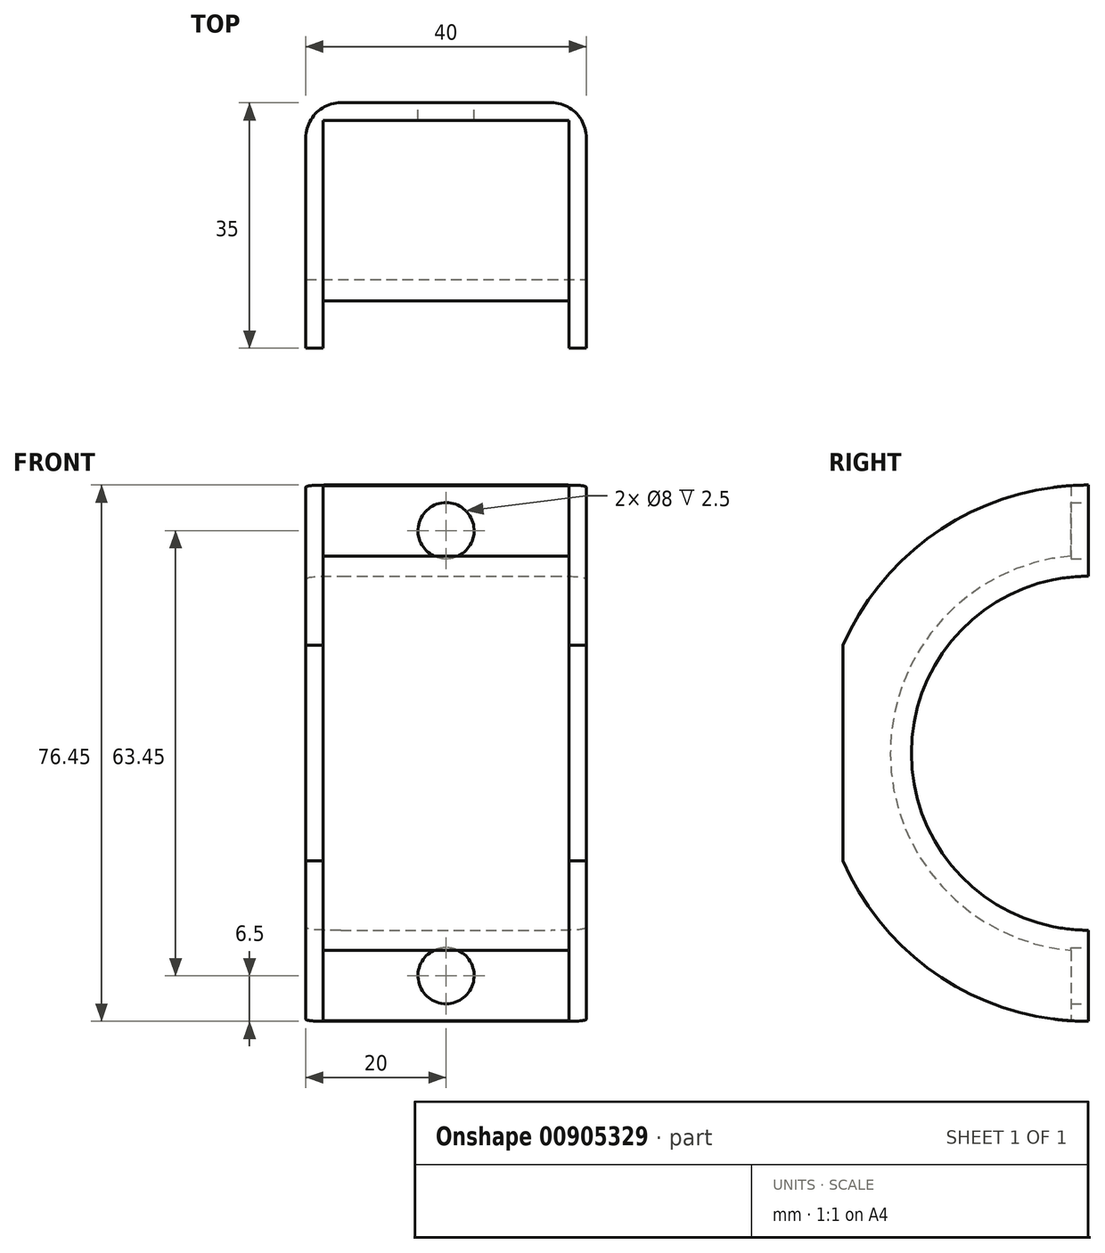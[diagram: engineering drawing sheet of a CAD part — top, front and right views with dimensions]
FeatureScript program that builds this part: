
annotation { "Feature Type Name" : "Feature", "Feature Type Description" : "" }
export const myFeature = defineFeature(function(context is Context, id is Id, definition is map)
    precondition{}
    {
        {
            var Q0;
            Q0=qCreatedBy(makeId("Top.planeOp"),FACE);
            var sketch = newSketch(context, id + "F0", { "sketchPlane" : qUnion([Q0])});
            skLineSegment(sketch, "E0.bottom", {"start": v(-20, 20) * mm, "end": v(20, 20) * mm});
            skLineSegment(sketch, "E0.top", {"start": v(-20, -20) * mm, "end": v(20, -20) * mm});
            skLineSegment(sketch, "E0.left", {"start": v(-20, 20) * mm, "end": v(-20, -20) * mm});
            skLineSegment(sketch, "E0.right", {"start": v(20, 20) * mm, "end": v(20, -20) * mm});
            skLineSegment(sketch, "E1.bottom", {"start": v(-17.5, 17.5) * mm, "end": v(17.5, 17.5) * mm});
            skLineSegment(sketch, "E1.top", {"start": v(-17.5, -17.5) * mm, "end": v(17.5, -17.5) * mm});
            skLineSegment(sketch, "E1.left", {"start": v(-17.5, 17.5) * mm, "end": v(-17.5, -17.5) * mm});
            skLineSegment(sketch, "E1.right", {"start": v(17.5, 17.5) * mm, "end": v(17.5, -17.5) * mm});
            skSolve(sketch);
        }
        {
            var Q0;
            Q0=qSketchRegion(id+"F0",true);
            extrude(context, id + "F1", {"entities" : qUnion([Q0]), "depth" : 100 * mm, "offsetDistance" : 25 * mm});
        }
        {
            var Q0;
            Q0=makeQuery(id+"F1.opExtrude","SWEPT_FACE",FACE,{"disambiguationData":[OSD([sQuery(id+"F0.wireOp",EDGE,"E0.right")])]});
            var sketch = newSketch(context, id + "F2", { "sketchPlane" : qUnion([Q0])});
            skArc(sketch, "E2", {"start": v(20, 75.8) * mm, "mid": v(-5.23, 50.57) * mm, "end": v(20, 25.34) * mm});
            skLineSegment(sketch, "E3", {"start": v(-20, 70.57) * mm, "end": v(-20, 30.57) * mm});
            skLineSegment(sketch, "E4", {"start": v(20, 22.34) * mm, "end": v(20, 12.34) * mm});
            skLineSegment(sketch, "E5", {"start": v(20, 78.8) * mm, "end": v(20, 88.8) * mm});
            skArc(sketch, "E6", {"start": v(20, 88.8) * mm, "mid": v(-0.9, 82.57) * mm, "end": v(-15, 65.93) * mm});
            skLineSegment(sketch, "E7.trimOffspring", {"start": v(20, 25.34) * mm, "end": v(20, 22.34) * mm});
            skArc(sketch, "E8", {"start": v(20, 78.8) * mm, "mid": v(-8.23, 50.57) * mm, "end": v(20, 22.34) * mm});
            skLineSegment(sketch, "E9", {"start": v(-15, 65.93) * mm, "end": v(-15, 35.2) * mm});
            skArc(sketch, "E10.trimOffspring", {"start": v(-15, 35.2) * mm, "mid": v(-0.9, 18.56) * mm, "end": v(20, 12.34) * mm});
            skPoint(sketch, "E11.orphan", {"position": v(-15, 50.57) * mm});
            skPoint(sketch, "E12.start.orphan", {"position": v(-20, 50.57) * mm});
            skPoint(sketch, "E13.orphan", {"position": v(-15, 76.8) * mm});
            skSolve(sketch);
        }
        {
            var Q0;
            {var subQ0=sQuery(id+"F2.wireOp",EDGE,"E2");Q0=makeQuery(id+"F2.imprint","IMPRINT",FACE,{"disambiguationData":[TD([[makeQuery(id+"F2.imprint","IMPRINT",EDGE,{"derivedFrom":subQ0}),1.0]])]});}
            var Q1;
            {var subQ0=sQuery(id+"F2.wireOp",EDGE,"E2");Q1=makeQuery(id+"F2.imprint","IMPRINT",FACE,{"disambiguationData":[TD([[makeQuery(id+"F2.imprint","IMPRINT",EDGE,{"derivedFrom":subQ0}),-1.0]])]});}
            var Q2;
            {var subQ0=sQuery(id+"F2.wireOp",EDGE,"xFw1aqm5-BAZR-JeNv-Sgt2-K9aK8hEqvfHp");Q2=makeQuery(id+"F2.imprint","IMPRINT",FACE,{"disambiguationData":[TD([[makeQuery(id+"F2.imprint","IMPRINT",EDGE,{"derivedFrom":subQ0}),1.0]])]});}
            var Q3;
            {var subQ0=sQuery(id+"F2.wireOp",EDGE,"6M1qleUD-lwjy-zaDF-z28L-FuXXR7HOL7hu");Q3=makeQuery(id+"F2.imprint","IMPRINT",FACE,{"disambiguationData":[TD([[makeQuery(id+"F2.imprint","IMPRINT",EDGE,{"derivedFrom":subQ0}),-1.0]])]});}
            extrude(context, id + "F3", {"entities" : qUnion([Q0, Q1, Q2, Q3]), "operationType" : NewBodyOperationType.REMOVE, "endBound" : BoundingType.THROUGH_ALL, "oppositeDirection" : true, "depth" : 25 * mm, "offsetDistance" : 25 * mm});
        }
        {
            var Q0;
            {var subQ0=sQuery(id+"F2.wireOp",EDGE,"E2");Q0=makeQuery(id+"F2.imprint","IMPRINT",FACE,{"disambiguationData":[TD([[makeQuery(id+"F2.imprint","IMPRINT",EDGE,{"derivedFrom":subQ0}),-1.0]])]});}
            extrude(context, id + "F4", {"entities" : qUnion([Q0]), "operationType" : NewBodyOperationType.ADD, "oppositeDirection" : true, "depth" : 40 * mm, "offsetDistance" : 25 * mm});
        }
        {
            var Q0;
            {var subQ0=sQuery(id+"F2.wireOp",EDGE,"bEhoVYsj-CkNL-EYDX-BTVM-B6UUKWKXnd8y");var subQ2=sQuery(id+"F0.wireOp",EDGE,"E0.bottom");var subQ3=sQuery(id+"F0.wireOp",EDGE,"E0.left");Q0=makeQuery(id+"F4.boolean.opBoolean","MERGE",EDGE,{"derivedFrom":[makeQuery(id+"F3.boolean.opBoolean","SPLIT",EDGE,{"disambiguationData":[TD([makeQuery(id+"F3.opExtrude","SWEPT_FACE",FACE,{"disambiguationData":[OSD([sQuery(id+"F2.wireOp",EDGE,"6M1qleUD-lwjy-zaDF-z28L-FuXXR7HOL7hu")])]})])],"derivedFrom":makeQuery(id+"F1.opExtrude","SWEPT_EDGE",EDGE,{"disambiguationData":[OSD([subQ2,subQ3])]})}),makeQuery(id+"F4.opExtrude","CAP_EDGE",EDGE,{"disambiguationData":[OSD([subQ0]),TDD([makeQuery(id+"F2.imprint","IMPRINT",EDGE,{"disambiguationData":[TD([[makeQuery(id+"F2.imprint","INTERSECT",VERTEX,{"disambiguationData":[OD(0.0)],"derivedFrom":[sQuery(id+"F2.wireOp",EDGE,"E2"),subQ0]}),1.0]])],"derivedFrom":subQ0})])],"isStart":false})]});}
            var Q1;
            {var subQ0=sQuery(id+"F2.wireOp",EDGE,"bEhoVYsj-CkNL-EYDX-BTVM-B6UUKWKXnd8y");var subQ2=sQuery(id+"F0.wireOp",EDGE,"E0.bottom");var subQ3=sQuery(id+"F0.wireOp",EDGE,"E0.left");Q1=makeQuery(id+"F4.boolean.opBoolean","MERGE",EDGE,{"derivedFrom":[makeQuery(id+"F3.boolean.opBoolean","SPLIT",EDGE,{"disambiguationData":[TD([makeQuery(id+"F3.opExtrude","SWEPT_FACE",FACE,{"disambiguationData":[OSD([sQuery(id+"F2.wireOp",EDGE,"xFw1aqm5-BAZR-JeNv-Sgt2-K9aK8hEqvfHp")])]})])],"derivedFrom":makeQuery(id+"F1.opExtrude","SWEPT_EDGE",EDGE,{"disambiguationData":[OSD([subQ2,subQ3])]})}),makeQuery(id+"F4.opExtrude","CAP_EDGE",EDGE,{"disambiguationData":[OSD([subQ0]),TDD([makeQuery(id+"F2.imprint","IMPRINT",EDGE,{"disambiguationData":[TD([[makeQuery(id+"F2.imprint","INTERSECT",VERTEX,{"disambiguationData":[OD(1.0)],"derivedFrom":[sQuery(id+"F2.wireOp",EDGE,"E2"),subQ0]}),-1.0]])],"derivedFrom":subQ0})])],"isStart":false})]});}
            var Q2;
            Q2=makeQuery(id+"F1.opExtrude","SWEPT_EDGE",EDGE,{"disambiguationData":[OSD([sQuery(id+"F0.wireOp",EDGE,"E0.top"),sQuery(id+"F0.wireOp",EDGE,"E0.left")])]});
            var Q3;
            Q3=makeQuery(id+"F1.opExtrude","SWEPT_EDGE",EDGE,{"disambiguationData":[OSD([sQuery(id+"F0.wireOp",EDGE,"E0.top"),sQuery(id+"F0.wireOp",EDGE,"E0.right")])]});
            var Q4;
            {var subQ0=sQuery(id+"F2.wireOp",EDGE,"bEhoVYsj-CkNL-EYDX-BTVM-B6UUKWKXnd8y");var subQ2=sQuery(id+"F0.wireOp",EDGE,"E0.bottom");var subQ3=sQuery(id+"F0.wireOp",EDGE,"E0.right");Q4=makeQuery(id+"F4.boolean.opBoolean","MERGE",EDGE,{"derivedFrom":[makeQuery(id+"F3.boolean.opBoolean","SPLIT",EDGE,{"disambiguationData":[TD([makeQuery(id+"F3.opExtrude","SWEPT_FACE",FACE,{"disambiguationData":[OSD([sQuery(id+"F2.wireOp",EDGE,"xFw1aqm5-BAZR-JeNv-Sgt2-K9aK8hEqvfHp")])]})])],"derivedFrom":makeQuery(id+"F1.opExtrude","SWEPT_EDGE",EDGE,{"disambiguationData":[OSD([subQ2,subQ3])]})}),makeQuery(id+"F4.opExtrude","CAP_EDGE",EDGE,{"disambiguationData":[OSD([subQ0]),TDD([makeQuery(id+"F2.imprint","IMPRINT",EDGE,{"disambiguationData":[TD([[makeQuery(id+"F2.imprint","INTERSECT",VERTEX,{"disambiguationData":[OD(1.0)],"derivedFrom":[sQuery(id+"F2.wireOp",EDGE,"E2"),subQ0]}),-1.0]])],"derivedFrom":subQ0})])],"isStart":true})]});}
            var Q5;
            {var subQ0=sQuery(id+"F2.wireOp",EDGE,"bEhoVYsj-CkNL-EYDX-BTVM-B6UUKWKXnd8y");var subQ2=sQuery(id+"F0.wireOp",EDGE,"E0.bottom");var subQ3=sQuery(id+"F0.wireOp",EDGE,"E0.right");Q5=makeQuery(id+"F4.boolean.opBoolean","MERGE",EDGE,{"derivedFrom":[makeQuery(id+"F3.boolean.opBoolean","SPLIT",EDGE,{"disambiguationData":[TD([makeQuery(id+"F3.opExtrude","SWEPT_FACE",FACE,{"disambiguationData":[OSD([sQuery(id+"F2.wireOp",EDGE,"6M1qleUD-lwjy-zaDF-z28L-FuXXR7HOL7hu")])]})])],"derivedFrom":makeQuery(id+"F1.opExtrude","SWEPT_EDGE",EDGE,{"disambiguationData":[OSD([subQ2,subQ3])]})}),makeQuery(id+"F4.opExtrude","CAP_EDGE",EDGE,{"disambiguationData":[OSD([subQ0]),TDD([makeQuery(id+"F2.imprint","IMPRINT",EDGE,{"disambiguationData":[TD([[makeQuery(id+"F2.imprint","INTERSECT",VERTEX,{"disambiguationData":[OD(0.0)],"derivedFrom":[sQuery(id+"F2.wireOp",EDGE,"E2"),subQ0]}),1.0]])],"derivedFrom":subQ0})])],"isStart":true})]});}
            fillet(context, id + "F5", {"entities" : qUnion([Q0, Q1, Q2, Q3, Q4, Q5]), "radius" : 5 * mm, "tangentPropagation" : true, "allowEdgeOverflow" : false});
        }
        {
            var Q0;
            {var subQ5=sQuery(id+"F2.wireOp",EDGE,"E3");Q0=makeQuery(id+"F2.imprint","IMPRINT",FACE,{"disambiguationData":[TD([[makeQuery(id+"F2.imprint","IMPRINT",EDGE,{"derivedFrom":subQ5}),1.0]])]});}
            extrude(context, id + "F6", {"entities" : qUnion([Q0]), "operationType" : NewBodyOperationType.REMOVE, "oppositeDirection" : true, "depth" : 40 * mm, "offsetDistance" : 25 * mm});
        }
        {
            var Q0;
            {var subQ0=sQuery(id+"F0.wireOp",EDGE,"E0.right");var subQ1=sQuery(id+"F0.wireOp",EDGE,"E0.bottom");var subQ2=sQuery(id+"F0.wireOp",EDGE,"E0.left");Q0=makeQuery(id+"F4.boolean.opBoolean","MERGE",EDGE,{"derivedFrom":[makeQuery(id+"F3.boolean.opBoolean","SPLIT",EDGE,{"disambiguationData":[TD([makeQuery(id+"F1.opExtrude","CAP_FACE",FACE,{"disambiguationData":[OSD([subQ1,sQuery(id+"F0.wireOp",EDGE,"E0.top"),subQ2,subQ0,sQuery(id+"F0.wireOp",EDGE,"E1.bottom"),sQuery(id+"F0.wireOp",EDGE,"E1.top"),sQuery(id+"F0.wireOp",EDGE,"E1.left"),sQuery(id+"F0.wireOp",EDGE,"E1.right")])],"isStart":false})])],"derivedFrom":makeQuery(id+"F1.opExtrude","SWEPT_EDGE",EDGE,{"disambiguationData":[OSD([subQ1,subQ2])]})}),makeQuery(id+"F4.opExtrude","CAP_EDGE",EDGE,{"disambiguationData":[OSD([subQ1,subQ0])],"isStart":false})]});}
            var Q1;
            {var subQ0=sQuery(id+"F0.wireOp",EDGE,"E0.right");var subQ1=sQuery(id+"F0.wireOp",EDGE,"E0.bottom");Q1=makeQuery(id+"F4.boolean.opBoolean","MERGE",EDGE,{"derivedFrom":[makeQuery(id+"F3.boolean.opBoolean","SPLIT",EDGE,{"disambiguationData":[TD([makeQuery(id+"F1.opExtrude","CAP_FACE",FACE,{"disambiguationData":[OSD([subQ1,sQuery(id+"F0.wireOp",EDGE,"E0.top"),sQuery(id+"F0.wireOp",EDGE,"E0.left"),subQ0,sQuery(id+"F0.wireOp",EDGE,"E1.bottom"),sQuery(id+"F0.wireOp",EDGE,"E1.top"),sQuery(id+"F0.wireOp",EDGE,"E1.left"),sQuery(id+"F0.wireOp",EDGE,"E1.right")])],"isStart":false})])],"derivedFrom":makeQuery(id+"F1.opExtrude","SWEPT_EDGE",EDGE,{"disambiguationData":[OSD([subQ1,subQ0])]})}),makeQuery(id+"F4.opExtrude","CAP_EDGE",EDGE,{"disambiguationData":[OSD([subQ1,subQ0])],"isStart":true})]});}
            var Q2;
            {var subQ0=sQuery(id+"F0.wireOp",EDGE,"E0.bottom");var subQ1=sQuery(id+"F0.wireOp",EDGE,"E0.left");Q2=makeQuery(id+"F4.boolean.opBoolean","MERGE",EDGE,{"derivedFrom":[makeQuery(id+"F3.boolean.opBoolean","SPLIT",EDGE,{"disambiguationData":[TD([makeQuery(id+"F1.opExtrude","CAP_FACE",FACE,{"disambiguationData":[OSD([subQ0,sQuery(id+"F0.wireOp",EDGE,"E0.top"),subQ1,sQuery(id+"F0.wireOp",EDGE,"E0.right"),sQuery(id+"F0.wireOp",EDGE,"E1.bottom"),sQuery(id+"F0.wireOp",EDGE,"E1.top"),sQuery(id+"F0.wireOp",EDGE,"E1.left"),sQuery(id+"F0.wireOp",EDGE,"E1.right")])],"isStart":true})])],"derivedFrom":makeQuery(id+"F1.opExtrude","SWEPT_EDGE",EDGE,{"disambiguationData":[OSD([subQ0,subQ1])]})}),makeQuery(id+"F4.opExtrude","CAP_EDGE",EDGE,{"disambiguationData":[OSD([sQuery(id+"F2.wireOp",EDGE,"E7.trimOffspring")])],"isStart":false})]});}
            var Q3;
            {var subQ0=sQuery(id+"F0.wireOp",EDGE,"E0.bottom");var subQ1=sQuery(id+"F0.wireOp",EDGE,"E0.right");Q3=makeQuery(id+"F4.boolean.opBoolean","MERGE",EDGE,{"derivedFrom":[makeQuery(id+"F3.boolean.opBoolean","SPLIT",EDGE,{"disambiguationData":[TD([makeQuery(id+"F1.opExtrude","CAP_FACE",FACE,{"disambiguationData":[OSD([subQ0,sQuery(id+"F0.wireOp",EDGE,"E0.top"),sQuery(id+"F0.wireOp",EDGE,"E0.left"),subQ1,sQuery(id+"F0.wireOp",EDGE,"E1.bottom"),sQuery(id+"F0.wireOp",EDGE,"E1.top"),sQuery(id+"F0.wireOp",EDGE,"E1.left"),sQuery(id+"F0.wireOp",EDGE,"E1.right")])],"isStart":true})])],"derivedFrom":makeQuery(id+"F1.opExtrude","SWEPT_EDGE",EDGE,{"disambiguationData":[OSD([subQ0,subQ1])]})}),makeQuery(id+"F4.opExtrude","CAP_EDGE",EDGE,{"disambiguationData":[OSD([sQuery(id+"F2.wireOp",EDGE,"E7.trimOffspring")])],"isStart":true})]});}
            fillet(context, id + "F7", {"entities" : qUnion([Q0, Q1, Q2, Q3]), "radius" : 5 * mm, "tangentPropagation" : true, "allowEdgeOverflow" : false});
        }
        {
            var Q0;
            {var subQ0=sQuery(id+"F0.wireOp",EDGE,"E0.right");var subQ1=sQuery(id+"F0.wireOp",EDGE,"E0.bottom");var subQ2=sQuery(id+"F0.wireOp",EDGE,"E0.left");Q0=makeQuery(id+"F4.boolean.opBoolean","MERGE",FACE,{"derivedFrom":[makeQuery(id+"F3.boolean.opBoolean","SPLIT",FACE,{"disambiguationData":[TD([makeQuery(id+"F1.opExtrude","CAP_FACE",FACE,{"disambiguationData":[OSD([subQ1,sQuery(id+"F0.wireOp",EDGE,"E0.top"),subQ2,subQ0,sQuery(id+"F0.wireOp",EDGE,"E1.bottom"),sQuery(id+"F0.wireOp",EDGE,"E1.top"),sQuery(id+"F0.wireOp",EDGE,"E1.left"),sQuery(id+"F0.wireOp",EDGE,"E1.right")])],"isStart":false})])],"derivedFrom":makeQuery(id+"F1.opExtrude","SWEPT_FACE",FACE,{"disambiguationData":[OSD([subQ1])]})}),makeQuery(id+"F4.opExtrude","SWEPT_FACE",FACE,{"disambiguationData":[OSD([subQ1,subQ0])]})]});}
            var sketch = newSketch(context, id + "F8", { "sketchPlane" : qUnion([Q0])});
            skLineSegment(sketch, "E14", {"start": v(0, 75.8) * mm, "end": v(0, 88.8) * mm});
            skCircle(sketch, "E15", {"center": v(0, 82.3) * mm, "radius": 4 * mm});
            skSolve(sketch);
        }
        {
            var Q0;
            Q0 = qSketchRegion(id + "F8", true);
            extrude(context, id + "F9", {"entities" : qUnion([Q0]), "operationType" : NewBodyOperationType.REMOVE, "oppositeDirection" : true, "depth" : 2.5 * mm, "offsetDistance" : 25 * mm});
        }
        {
            var Q0;
            {var subQ0=sQuery(id+"F0.wireOp",EDGE,"E0.right");var subQ1=sQuery(id+"F0.wireOp",EDGE,"E0.left");var subQ2=sQuery(id+"F0.wireOp",EDGE,"E0.bottom");Q0=makeQuery(id+"F4.boolean.opBoolean","MERGE",FACE,{"derivedFrom":[makeQuery(id+"F3.boolean.opBoolean","SPLIT",FACE,{"disambiguationData":[TD([makeQuery(id+"F1.opExtrude","CAP_FACE",FACE,{"disambiguationData":[OSD([subQ2,sQuery(id+"F0.wireOp",EDGE,"E0.top"),subQ1,subQ0,sQuery(id+"F0.wireOp",EDGE,"E1.bottom"),sQuery(id+"F0.wireOp",EDGE,"E1.top"),sQuery(id+"F0.wireOp",EDGE,"E1.left"),sQuery(id+"F0.wireOp",EDGE,"E1.right")])],"isStart":true})])],"derivedFrom":makeQuery(id+"F1.opExtrude","SWEPT_FACE",FACE,{"disambiguationData":[OSD([subQ2])]})}),makeQuery(id+"F4.opExtrude","SWEPT_FACE",FACE,{"disambiguationData":[OSD([sQuery(id+"F2.wireOp",EDGE,"E7.trimOffspring")])]})]});}
            var sketch = newSketch(context, id + "F10", { "sketchPlane" : qUnion([Q0])});
            skLineSegment(sketch, "E16", {"start": v(0, 12.34) * mm, "end": v(0, 25.34) * mm});
            skCircle(sketch, "E17", {"center": v(0, 18.84) * mm, "radius": 4 * mm});
            skSolve(sketch);
        }
        {
            var Q0;
            Q0 = qSketchRegion(id + "F10", true);
            extrude(context, id + "F11", {"entities" : qUnion([Q0]), "operationType" : NewBodyOperationType.REMOVE, "oppositeDirection" : true, "depth" : 2.5 * mm, "offsetDistance" : 25 * mm});
        }
    });
